FCSTD DOCUMENT  (FreeCAD 0.19R24366 (Git))
Label: Dual strain solver common pivot
License: All rights reserved
LicenseURL: http://en.wikipedia.org/wiki/All_rights_reserved
objects: Sketcher::SketchObject×1, PartDesign::Body×1
note: 2 computed .brp shape members not serialized (recipe doc carries the construction recipe); baked Part::Feature solids carry a one-line shape summary decoded from their .brp

FEATURE [Sketcher::SketchObject] Sketch
  FullyConstrained = true
  MapMode = 5
  Support = -> [XY_Plane]
  sketch-geometry (39):
    g0: LineSegment StartX=710.218 StartY=0 StartZ=0 EndX=730.218 EndY=49.6456 EndZ=0
    g1: LineSegment StartX=750.218 StartY=0 StartZ=0 EndX=730.218 EndY=49.6456 EndZ=0
    g2: LineSegment StartX=430.41 StartY=316.58 StartZ=0 EndX=730.218 EndY=49.6456 EndZ=0
    g3: LineSegment StartX=699.176 StartY=449.865 StartZ=0 EndX=730.218 EndY=49.6456 EndZ=0
    g4: LineSegment StartX=730.218 StartY=49.6456 StartZ=0 EndX=737.691 EndY=68.1968 EndZ=0
    g5: LineSegment StartX=730.218 StartY=49.6456 StartZ=0 EndX=722.744 EndY=68.1968 EndZ=0
    g6: LineSegment StartX=737.691 StartY=68.1968 StartZ=0 EndX=728.491 EndY=71.903 EndZ=0
    g7: LineSegment StartX=722.744 StartY=68.1968 StartZ=0 EndX=713.545 EndY=64.4907 EndZ=0
    g8: LineSegment StartX=0 StartY=-800 StartZ=0 EndX=750.218 EndY=-800 EndZ=0
    g9: LineSegment StartX=418.419 StartY=-496.011 StartZ=0 EndX=711.245 EndY=-627.334 EndZ=0
    g10: LineSegment StartX=711.245 StartY=-627.334 StartZ=0 EndX=750.218 EndY=-800 EndZ=0
    g11: LineSegment StartX=695.332 StartY=-362.449 StartZ=0 EndX=722.367 EndY=-682.233 EndZ=0
    g12: LineSegment StartX=722.367 StartY=-682.233 StartZ=0 EndX=590.218 EndY=-800 EndZ=0
    g13: LineSegment StartX=722.367 StartY=-682.233 StartZ=0 EndX=737.298 EndY=-668.927 EndZ=0
    g14: LineSegment StartX=711.245 StartY=-627.334 StartZ=0 EndX=706.841 EndY=-607.825 EndZ=0
    g15: LineSegment StartX=737.298 StartY=-668.927 StartZ=0 EndX=719.559 EndY=-649.022 EndZ=0
    g16: LineSegment StartX=706.841 StartY=-607.825 StartZ=0 EndX=680.833 EndY=-613.695 EndZ=0
    g17: LineSegment StartX=0 StartY=0 StartZ=0 EndX=750.218 EndY=0 EndZ=0
    g18: LineSegment StartX=750.218 StartY=0 StartZ=0 EndX=750.218 EndY=-800 EndZ=0
    g19: LineSegment StartX=0 StartY=-800 StartZ=0 EndX=722.367 EndY=-682.233 EndZ=0
    g20: LineSegment StartX=711.245 StartY=-627.334 StartZ=0 EndX=0 EndY=-800 EndZ=0
    g21: LineSegment StartX=0 StartY=0 StartZ=0 EndX=-6.78308 EndY=99.7697 EndZ=0
    g22: LineSegment StartX=0 StartY=-800 StartZ=0 EndX=-16.0905 EndY=-701.303 EndZ=0
    g23: LineSegment StartX=0 StartY=-800 StartZ=0 EndX=-23.5913 EndY=-702.823 EndZ=0
    g24: LineSegment StartX=-16.0905 StartY=-701.303 StartZ=0 EndX=695.332 EndY=-362.449 EndZ=0
    g25: LineSegment StartX=418.419 StartY=-496.011 StartZ=0 EndX=-23.5913 EndY=-702.823 EndZ=0
    g26: LineSegment StartX=699.176 StartY=449.865 StartZ=0 EndX=-6.78308 EndY=99.7697 EndZ=0
    g27: LineSegment StartX=430.41 StartY=316.58 StartZ=0 EndX=-6.78308 EndY=99.7697 EndZ=0
    g28: LineSegment StartX=0 StartY=0 StartZ=0 EndX=730.218 EndY=49.6456 EndZ=0
    g29: LineSegment StartX=730.218 StartY=49.6456 StartZ=0 EndX=0 EndY=0 EndZ=0
    g30: LineSegment StartX=-6.78308 StartY=99.7697 StartZ=0 EndX=0 EndY=0 EndZ=0
    g31: LineSegment StartX=730.218 StartY=49.6456 StartZ=0 EndX=730.218 EndY=0 EndZ=0
    g32: LineSegment StartX=730.218 StartY=49.6456 StartZ=0 EndX=730.218 EndY=0 EndZ=0
    g33: LineSegment StartX=430.41 StartY=316.58 StartZ=0 EndX=452.624 EndY=271.785 EndZ=0
    g34: LineSegment StartX=699.176 StartY=449.865 StartZ=0 EndX=721.39 EndY=405.07 EndZ=0
    g35: LineSegment StartX=452.624 StartY=271.785 StartZ=0 EndX=470.669 EndY=280.734 EndZ=0
    g36: LineSegment StartX=721.39 StartY=405.07 StartZ=0 EndX=703.344 EndY=396.121 EndZ=0
    g37: LineSegment StartX=710.218 StartY=0 StartZ=0 EndX=699.176 EndY=449.865 EndZ=0
    g38: LineSegment StartX=590.218 StartY=-800 StartZ=0 EndX=695.332 EndY=-362.449 EndZ=0
  constraints (112):
    c: PointOnObject(g0,g-1)
    c: PointOnObject(g1,g-1)
    c: Equal(g0,g1)
    c: Coincident(g2,g1)
    c: Coincident(g3,g0)
    c: Coincident(g4,g0)
    c: Coincident(g5,g1)
    c: Distance(g4) = 20
    c: Parallel(g0,g4)
    c: Parallel(g1,g5)
    c: Coincident(g6,g4)
    c: PointOnObject(g6,g3)
    c: Coincident(g7,g5)
    c: PointOnObject(g7,g2)
    c: Perpendicular(g7,g5)
    c: Perpendicular(g6,g4)
    c: Equal(g6,g7)
    c: Equal(g2,g3)
    c: Distance(g0,g3) = 450  'LEVER ARM LENGTH'
    c: Horizontal(g8)
    c: Coincident(g10,g9)
    c: Coincident(g12,g11)
    c: PointOnObject(g12,g8)
    c: Coincident(g13,g11)
    c: Coincident(g14,g9)
    c: Parallel(g12,g13)
    c: Parallel(g10,g14)
    c: Coincident(g15,g13)
    c: PointOnObject(g15,g11)
    c: Coincident(g16,g14)
    c: PointOnObject(g16,g9)
    c: Perpendicular(g14,g16)
    c: Perpendicular(g15,g13)
    c: Equal(g15,g16)
    c: Equal(g11,g9)
    c: Equal(g12,g10)
    c: Coincident(g8,g10)
    c: Coincident(g17,g1)
    c: DistanceX(g0,g1) = 40  'MIN STRAIN'
    c: DistanceX(g12,g8) = 160  'MAX STRAIN'
    c: Equal(g8,g17)
    c: DistanceX(g17,g17) = 750.218  'ACTUATOR - END POINT'
    c: Equal(g5,g4)
    c: Equal(g13,g14)
    c: Equal(g13,g4)
    c: Coincident(g18,g1)
    c: Coincident(g18,g8)
    c: DistanceY(g8,g-1) = 800
    c: Coincident(g19,g8)
    c: Coincident(g19,g11)
    c: Coincident(g20,g9)
    c: Coincident(g20,g8)
    c: Coincident(g17,g-1)
    c: Coincident(g21,g17)
    c: Coincident(g22,g8)
    c: Coincident(g23,g8)
    c: PointOnObject(g8,g-2)
    c: Perpendicular(g19,g22)
    c: Perpendicular(g23,g20)
    c: Distance(g21) = 100
    c: Equal(g23,g22)
    c: Coincident(g24,g22)
    c: Coincident(g24,g11)
    c: Coincident(g25,g9)
    c: Coincident(g25,g23)
    c: Coincident(g26,g3)
    c: Coincident(g26,g21)
    c: Coincident(g27,g2)
    c: Coincident(g28,g17)
    c: Coincident(g28,g0)
    c: Coincident(g29,g1)
    c: Coincident(g29,g17)
    c: Coincident(g30,g27)
    c: Coincident(g30,g17)
    c: Equal(g30,g21)
    c: Perpendicular(g21,g28)
    c: Perpendicular(g30,g29)
    c: Distance(g26) = 788
    c: Distance(g27) = 488
    c: Equal(g26,g24)
    c: Equal(g27,g25)
    c: Equal(g28,g29)
    c: Equal(g29,g20)
    c: Equal(g20,g19)
    c: Coincident(g31,g1)
    c: PointOnObject(g31,g17)
    c: Vertical(g31)
    c: Coincident(g32,g0)
    c: PointOnObject(g32,g17)
    c: Vertical(g32)
    c: Equal(g31,g32)  'LOCK SMALL STRAIN SLIDER EQUAL ANGLE'
    c: Coincident(g33,g2)
    c: Coincident(g34,g3)
    c: Perpendicular(g27,g33)
    c: Perpendicular(g34,g26)
    c: Distance(g33) = 50
    c: Equal(g33,g34)
    c: Coincident(g35,g33)
    c: PointOnObject(g35,g2)
    c: Coincident(g36,g34)
    c: PointOnObject(g36,g3)
    c: Perpendicular(g35,g33)
    c: Perpendicular(g34,g36)
    c: Equal(g35,g36)  'LOCK SMALL STRAIN ACTUATOR EQUAL ANGLE'
    c: Equal(g21,g23)
    c: Coincident(g37,g0)
    c: Coincident(g38,g12)
    c: Coincident(g38,g11)
    c: Equal(g37,g38)
    c: Coincident(g3,g37)
    c: Distance(g28) = 731.904
    c: DistanceY(g31,g31) = 49.6456
FEATURE [PartDesign::Body] Body
  Group = -> [Sketch]
  Origin = -> Origin
